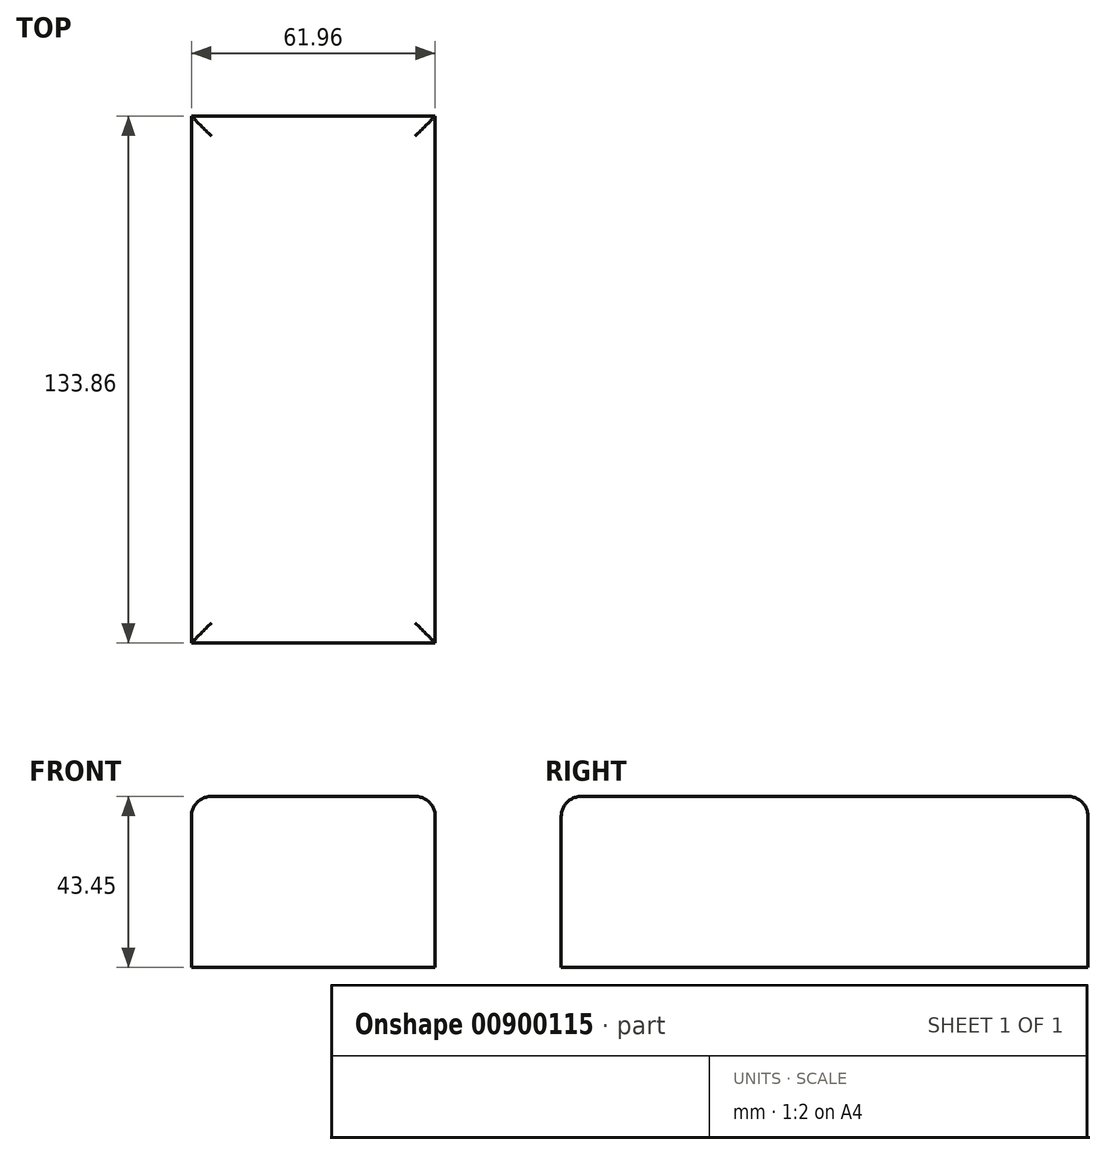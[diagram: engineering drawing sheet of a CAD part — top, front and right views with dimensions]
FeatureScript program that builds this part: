
annotation { "Feature Type Name" : "Feature", "Feature Type Description" : "" }
export const myFeature = defineFeature(function(context is Context, id is Id, definition is map)
    precondition{}
    {
        {
            var Q0;
            Q0=qCreatedBy(makeId("Front.planeOp"),FACE);
            var sketch = newSketch(context, id + "F0", { "sketchPlane" : qUnion([Q0])});
            skLineSegment(sketch, "E0.bottom", {"start": v(0, 0) * mm, "end": v(61.96, 0) * mm});
            skLineSegment(sketch, "E0.top", {"start": v(0, 43.45) * mm, "end": v(61.96, 43.45) * mm});
            skLineSegment(sketch, "E0.left", {"start": v(0, 0) * mm, "end": v(0, 43.45) * mm});
            skLineSegment(sketch, "E0.right", {"start": v(61.96, 0) * mm, "end": v(61.96, 43.45) * mm});
            skSolve(sketch);
        }
        {
            var Q0;
            Q0=makeQuery(id+"F0.imprint","IMPRINT",FACE,{"disambiguationData":[TD([[makeQuery(id+"F0.imprint","IMPRINT",EDGE,{"derivedFrom":sQuery(id+"F0.wireOp",EDGE,"E0.bottom")}),1.0]])]});
            extrude(context, id + "F1", {"entities" : qUnion([Q0]), "oppositeDirection" : true, "depth" : 133.86 * mm, "offsetDistance" : 25.4 * mm});
        }
        {
            var Q0;
            Q0=makeQuery(id+"F1.opExtrude","SWEPT_EDGE",EDGE,{"disambiguationData":[OSD([sQuery(id+"F0.wireOp",EDGE,"E0.top"),sQuery(id+"F0.wireOp",EDGE,"E0.right")])]});
            var Q1;
            Q1=makeQuery(id+"F1.opExtrude","SWEPT_FACE",FACE,{"disambiguationData":[OSD([sQuery(id+"F0.wireOp",EDGE,"E0.top")])]});
            fillet(context, id + "F2", {"entities" : qUnion([Q0, Q1]), "radius" : 5.08 * mm, "tangentPropagation" : true, "allowEdgeOverflow" : false});
        }
    });
